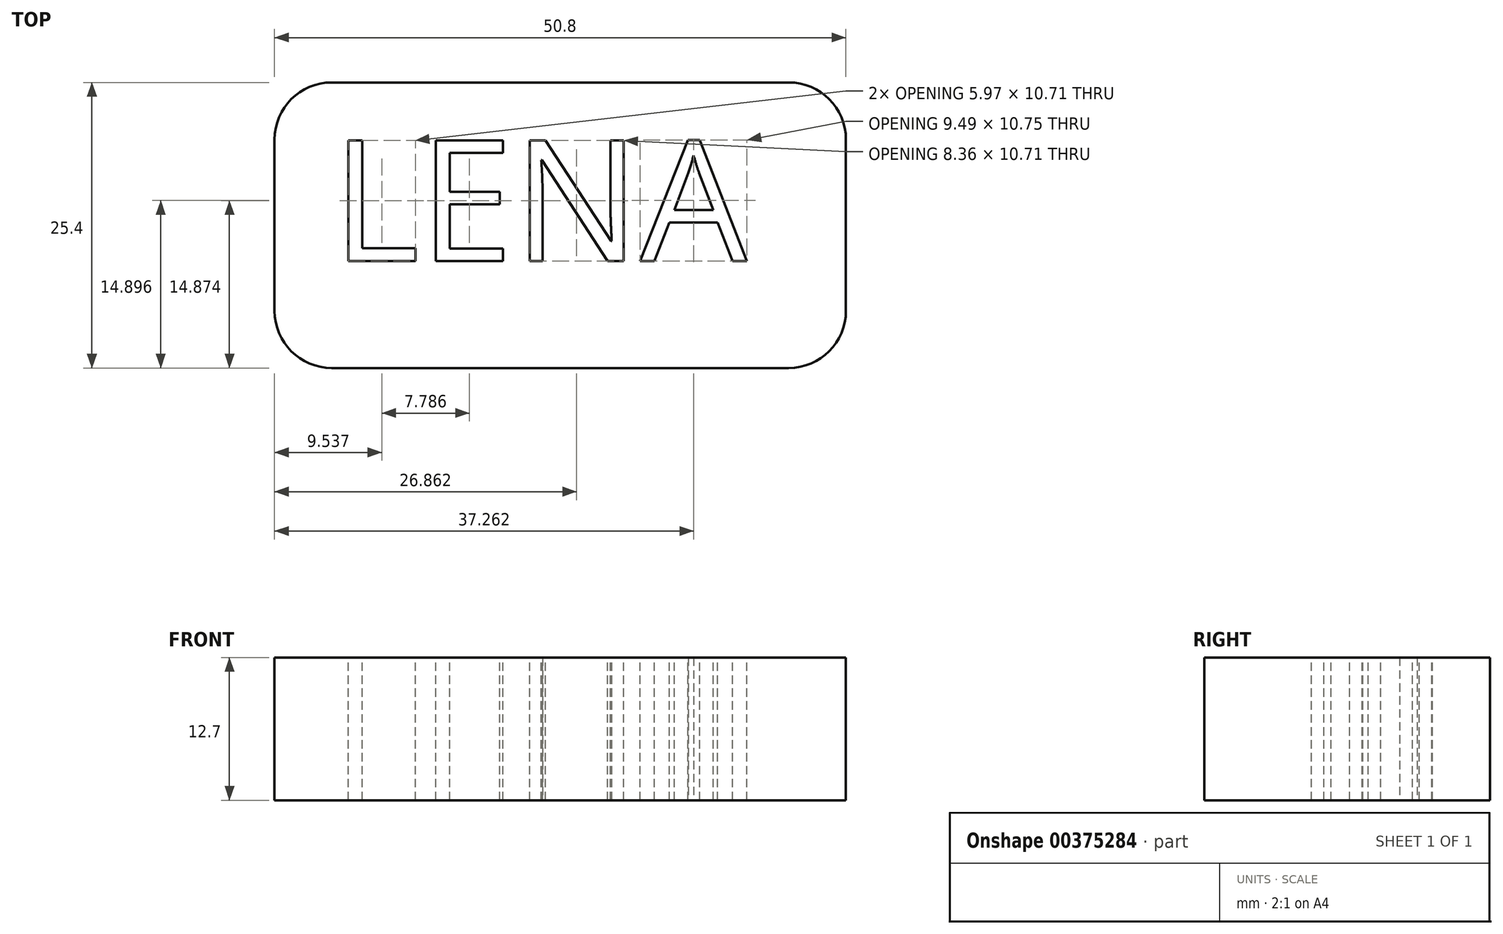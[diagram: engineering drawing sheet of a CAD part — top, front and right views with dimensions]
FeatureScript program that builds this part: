
annotation { "Feature Type Name" : "Feature", "Feature Type Description" : "" }
export const myFeature = defineFeature(function(context is Context, id is Id, definition is map)
    precondition{}
    {
        {
            var Q0;
            Q0=qCreatedBy(makeId("Top.planeOp"),FACE);
            var sketch = newSketch(context, id + "F0", { "sketchPlane" : qUnion([Q0])});
            skLineSegment(sketch, "E0", {"start": v(0, 0) * mm, "end": v(0, 25.4) * mm});
            skLineSegment(sketch, "E1", {"start": v(0, 25.4) * mm, "end": v(50.8, 25.4) * mm});
            skLineSegment(sketch, "E2", {"start": v(50.8, 25.4) * mm, "end": v(50.8, 0) * mm});
            skLineSegment(sketch, "E3", {"start": v(50.8, 0) * mm, "end": v(0, 0) * mm});
            skSolve(sketch);
        }
        {
            var Q0;
            Q0 = qSketchRegion(id + "F0", true);
            extrude(context, id + "F1", {"entities" : qUnion([Q0]), "depth" : 12.7 * mm});
        }
        {
            var Q0;
            Q0=makeQuery(id+"F1.opExtrude","SWEPT_EDGE",EDGE,{"disambiguationData":[OSD([sQuery(id+"F0.wireOp",EDGE,"E0"),sQuery(id+"F0.wireOp",EDGE,"E3")])]});
            var Q1;
            Q1=makeQuery(id+"F1.opExtrude","SWEPT_EDGE",EDGE,{"disambiguationData":[OSD([sQuery(id+"F0.wireOp",EDGE,"E2"),sQuery(id+"F0.wireOp",EDGE,"E3")])]});
            var Q2;
            Q2=makeQuery(id+"F1.opExtrude","SWEPT_EDGE",EDGE,{"disambiguationData":[OSD([sQuery(id+"F0.wireOp",EDGE,"E1"),sQuery(id+"F0.wireOp",EDGE,"E2")])]});
            var Q3;
            Q3=makeQuery(id+"F1.opExtrude","SWEPT_EDGE",EDGE,{"disambiguationData":[OSD([sQuery(id+"F0.wireOp",EDGE,"E0"),sQuery(id+"F0.wireOp",EDGE,"E1")])]});
            fillet(context, id + "F2", {"entities" : qUnion([Q0, Q1, Q2, Q3]), "radius" : 5.08 * mm, "tangentPropagation" : true, "allowEdgeOverflow" : false});
        }
        {
            var Q0;
            Q0=makeQuery(id+"F1.opExtrude","CAP_FACE",FACE,{"disambiguationData":[OSD([sQuery(id+"F0.wireOp",EDGE,"E0"),sQuery(id+"F0.wireOp",EDGE,"E1"),sQuery(id+"F0.wireOp",EDGE,"E2"),sQuery(id+"F0.wireOp",EDGE,"E3")])],"isStart":false});
            var sketch = newSketch(context, id + "F3", { "sketchPlane" : qUnion([Q0])});
            skText(sketch, "E4", { "text": "LENA", "fontName": "OpenSans-Regular.ttf"});
            const initialGuessF3  = {"E4": [0.00508, 0.00952, 1, 0, 0.0108]};
            skSetInitialGuess(sketch, initialGuessF3);
            skSolve(sketch);
        }
        {
            var Q0;
            Q0 = qSketchRegion(id + "F3", true);
            extrude(context, id + "F4", {"entities" : qUnion([Q0]), "operationType" : NewBodyOperationType.REMOVE, "oppositeDirection" : true, "depth" : 25.4 * mm});
        }
    });
